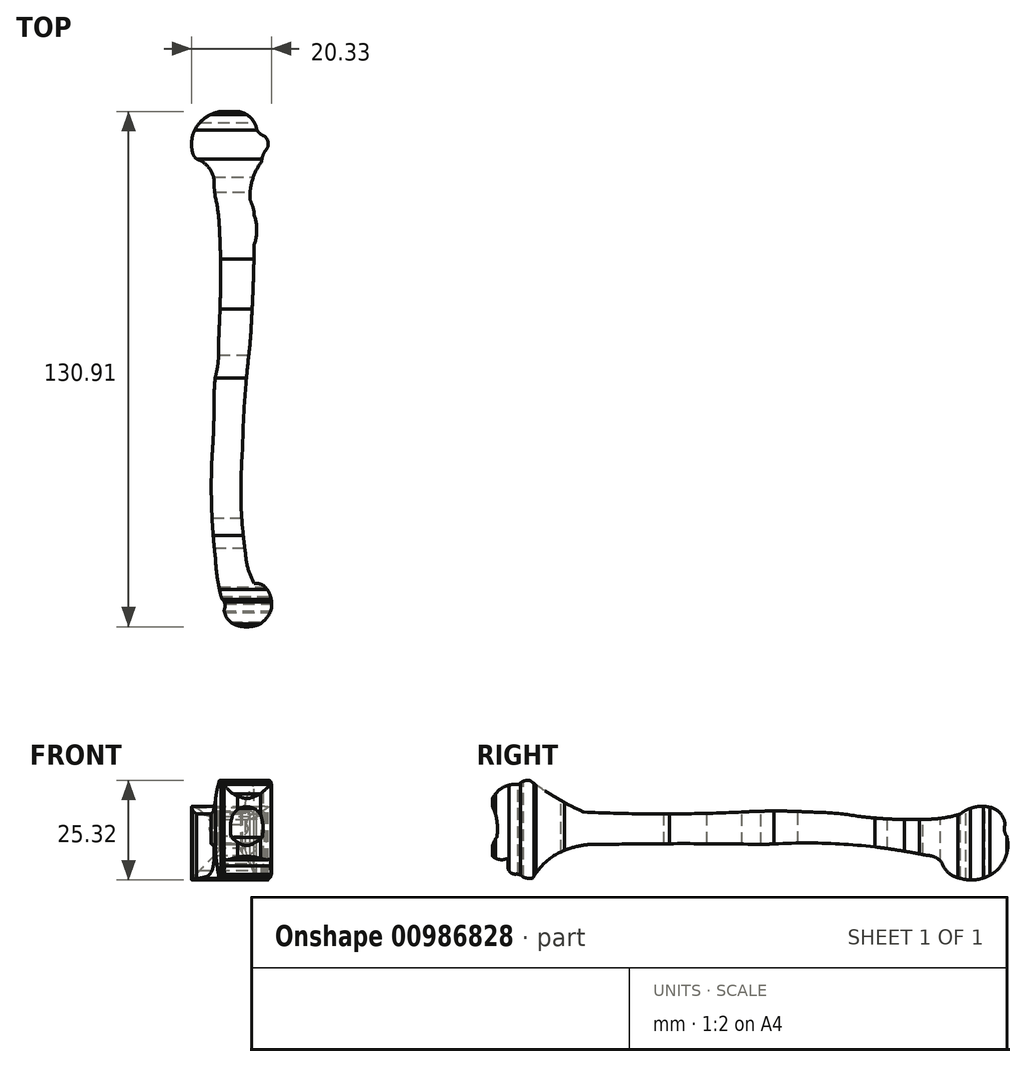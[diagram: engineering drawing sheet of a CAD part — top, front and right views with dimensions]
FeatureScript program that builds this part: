
annotation { "Feature Type Name" : "Feature", "Feature Type Description" : "" }
export const myFeature = defineFeature(function(context is Context, id is Id, definition is map)
    precondition{}
    {
        {
            var Q0;
            Q0=qCreatedBy(makeId("Top.planeOp"),FACE);
            var sketch = newSketch(context, id + "F0", { "sketchPlane" : qUnion([Q0])});
            skSolve(sketch);
        }
        {
            var Q0;
            Q0=qCreatedBy(makeId("Top.planeOp"),FACE);
            var sketch = newSketch(context, id + "F1", { "sketchPlane" : qUnion([Q0])});
            skArc(sketch, "E0", {"start": v(-3.52, 66.02) * mm, "mid": v(-7.2, 63.97) * mm, "end": v(-9.46, 60.42) * mm});
            skArc(sketch, "E1", {"start": v(3.16, 66.02) * mm, "mid": v(-0.18, 66.65) * mm, "end": v(-3.52, 66.02) * mm});
            skArc(sketch, "E2", {"start": v(-9.46, 60.42) * mm, "mid": v(-9.76, 58.04) * mm, "end": v(-9.46, 55.66) * mm});
            skArc(sketch, "E3", {"start": v(-9.46, 55.66) * mm, "mid": v(-9.1, 54.9) * mm, "end": v(-8.52, 54.28) * mm});
            skArc(sketch, "E4", {"start": v(-4.09, 49.15) * mm, "mid": v(-5.6, 52.32) * mm, "end": v(-8.52, 54.28) * mm});
            skArc(sketch, "E5", {"start": v(-4.09, 49.15) * mm, "mid": v(-4.02, 46.94) * mm, "end": v(-3.74, 44.74) * mm});
            skArc(sketch, "E6", {"start": v(-2.67, 35.74) * mm, "mid": v(-2.98, 40.27) * mm, "end": v(-3.74, 44.74) * mm});
            skArc(sketch, "E7", {"start": v(-2.38, 23.8) * mm, "mid": v(-2.43, 29.77) * mm, "end": v(-2.67, 35.74) * mm});
            skArc(sketch, "E8", {"start": v(-2.67, 12.98) * mm, "mid": v(-2.48, 18.39) * mm, "end": v(-2.38, 23.8) * mm});
            skArc(sketch, "E9", {"start": v(-2.67, 12.98) * mm, "mid": v(-2.88, 8.26) * mm, "end": v(-2.96, 3.53) * mm});
            skArc(sketch, "E10", {"start": v(-3.74, -1.22) * mm, "mid": v(-3.23, 1.14) * mm, "end": v(-2.96, 3.53) * mm});
            skArc(sketch, "E11", {"start": v(-3.74, -1.22) * mm, "mid": v(-4.07, -5.7) * mm, "end": v(-4.09, -10.2) * mm});
            skArc(sketch, "E12", {"start": v(-4.55, -21.07) * mm, "mid": v(-4.23, -15.64) * mm, "end": v(-4.09, -10.2) * mm});
            skArc(sketch, "E13", {"start": v(-4.55, -21.07) * mm, "mid": v(-4.69, -34.17) * mm, "end": v(-3.7, -47.24) * mm});
            skArc(sketch, "E14", {"start": v(-3.7, -47.24) * mm, "mid": v(-3.27, -52.02) * mm, "end": v(-2.32, -56.73) * mm});
            skArc(sketch, "E15", {"start": v(-2.32, -56.73) * mm, "mid": v(-2.02, -57.54) * mm, "end": v(-1.48, -58.22) * mm});
            skArc(sketch, "E16", {"start": v(-1.48, -60.4) * mm, "mid": v(-1.26, -59.31) * mm, "end": v(-1.48, -58.22) * mm});
            skArc(sketch, "E17", {"start": v(-1.48, -60.4) * mm, "mid": v(-0.4, -62.89) * mm, "end": v(1.9, -64.3) * mm});
            skArc(sketch, "E18", {"start": v(1.9, -64.3) * mm, "mid": v(4.86, -64.6) * mm, "end": v(7.73, -63.87) * mm});
            skArc(sketch, "E19", {"start": v(7.73, -63.87) * mm, "mid": v(9.34, -62.34) * mm, "end": v(10.43, -60.4) * mm});
            skArc(sketch, "E20", {"start": v(10.43, -60.4) * mm, "mid": v(10.57, -58.97) * mm, "end": v(10.43, -57.53) * mm});
            skArc(sketch, "E21", {"start": v(10.43, -57.53) * mm, "mid": v(9.75, -55.62) * mm, "end": v(8.46, -54.07) * mm});
            skArc(sketch, "E22", {"start": v(8.46, -54.07) * mm, "mid": v(7.35, -53.68) * mm, "end": v(6.17, -53.63) * mm});
            skArc(sketch, "E23", {"start": v(3.98, -46.38) * mm, "mid": v(4.67, -50.13) * mm, "end": v(6.17, -53.63) * mm});
            skArc(sketch, "E24", {"start": v(3.19, -19.72) * mm, "mid": v(2.8, -33.07) * mm, "end": v(3.98, -46.38) * mm});
            skArc(sketch, "E25", {"start": v(5.07, 6.86) * mm, "mid": v(3.76, -6.4) * mm, "end": v(3.19, -19.72) * mm});
            skArc(sketch, "E26", {"start": v(5.07, 6.86) * mm, "mid": v(5.78, 19.65) * mm, "end": v(6.17, 32.46) * mm});
            skArc(sketch, "E27", {"start": v(6.17, 32.46) * mm, "mid": v(6.77, 36.22) * mm, "end": v(6.17, 39.98) * mm});
            skArc(sketch, "E28", {"start": v(6.17, 39.98) * mm, "mid": v(5.84, 41.97) * mm, "end": v(5.07, 43.82) * mm});
            skArc(sketch, "E29", {"start": v(6.76, 61.78) * mm, "mid": v(5.55, 64.4) * mm, "end": v(3.16, 66.02) * mm});
            skArc(sketch, "E30", {"start": v(6.76, 61.78) * mm, "mid": v(7.56, 60.7) * mm, "end": v(8.73, 60.07) * mm});
            skArc(sketch, "E31", {"start": v(9.28, 56.71) * mm, "mid": v(9.69, 58.5) * mm, "end": v(8.73, 60.07) * mm});
            skArc(sketch, "E32", {"start": v(9.28, 56.71) * mm, "mid": v(8.4, 55.25) * mm, "end": v(8.04, 53.58) * mm});
            skArc(sketch, "E33", {"start": v(8.04, 53.58) * mm, "mid": v(5.7, 48.96) * mm, "end": v(5.07, 43.82) * mm});
            skSolve(sketch);
        }
        {
            var Q0;
            Q0=qCreatedBy(makeId("Right.planeOp"),FACE);
            var sketch = newSketch(context, id + "F2", { "sketchPlane" : qUnion([Q0])});
            skArc(sketch, "E34", {"start": v(63.48, -25.15) * mm, "mid": v(65.94, -21.14) * mm, "end": v(65.99, -16.45) * mm});
            skArc(sketch, "E35", {"start": v(54.23, -27.19) * mm, "mid": v(59.12, -27.37) * mm, "end": v(63.48, -25.15) * mm});
            skArc(sketch, "E36", {"start": v(49.6, -23.4) * mm, "mid": v(51.42, -25.9) * mm, "end": v(54.23, -27.19) * mm});
            skArc(sketch, "E37", {"start": v(49.6, -23.4) * mm, "mid": v(47.96, -21.88) * mm, "end": v(45.78, -21.37) * mm});
            skArc(sketch, "E38", {"start": v(65.57, -13.52) * mm, "mid": v(65.4, -15.03) * mm, "end": v(65.99, -16.45) * mm});
            skArc(sketch, "E39", {"start": v(65.57, -13.52) * mm, "mid": v(64.36, -10.62) * mm, "end": v(61.62, -9.1) * mm});
            skArc(sketch, "E40", {"start": v(61.62, -9.1) * mm, "mid": v(57.72, -9.1) * mm, "end": v(54.23, -10.84) * mm});
            skArc(sketch, "E41", {"start": v(46.71, -12.16) * mm, "mid": v(50.51, -11.74) * mm, "end": v(54.23, -10.84) * mm});
            skArc(sketch, "E42", {"start": v(45.78, -21.37) * mm, "mid": v(25.17, -18.55) * mm, "end": v(4.38, -18.58) * mm});
            skArc(sketch, "E43", {"start": v(4.38, -18.58) * mm, "mid": v(-16.31, -18.36) * mm, "end": v(-37, -18.58) * mm});
            skArc(sketch, "E44", {"start": v(-37, -18.58) * mm, "mid": v(-40.84, -18.66) * mm, "end": v(-44.6, -19.45) * mm});
            skArc(sketch, "E45", {"start": v(-44.6, -19.45) * mm, "mid": v(-50.3, -22.33) * mm, "end": v(-54.45, -27.19) * mm});
            skArc(sketch, "E46", {"start": v(-60.75, -24) * mm, "mid": v(-60.66, -23.06) * mm, "end": v(-61, -22.19) * mm});
            skArc(sketch, "E47", {"start": v(-64.85, -21.37) * mm, "mid": v(-63.06, -22.38) * mm, "end": v(-61, -22.19) * mm});
            skArc(sketch, "E48", {"start": v(-63.55, -16.72) * mm, "mid": v(-64.64, -18.92) * mm, "end": v(-64.85, -21.37) * mm});
            skArc(sketch, "E49", {"start": v(-63.55, -16.72) * mm, "mid": v(-63.45, -13) * mm, "end": v(-64.44, -9.4) * mm});
            skArc(sketch, "E50", {"start": v(-63.93, -5.77) * mm, "mid": v(-64.77, -7.5) * mm, "end": v(-64.44, -9.4) * mm});
            skArc(sketch, "E51", {"start": v(-60.75, -24) * mm, "mid": v(-60.25, -25.52) * mm, "end": v(-58.78, -26.13) * mm});
            skArc(sketch, "E52", {"start": v(-56.87, -26.86) * mm, "mid": v(-57.73, -26.24) * mm, "end": v(-58.78, -26.13) * mm});
            skArc(sketch, "E53", {"start": v(-56.87, -26.86) * mm, "mid": v(-55.68, -27.16) * mm, "end": v(-54.45, -27.19) * mm});
            skArc(sketch, "E54", {"start": v(-58.3, -3.32) * mm, "mid": v(-61.43, -3.82) * mm, "end": v(-63.93, -5.77) * mm});
            skArc(sketch, "E55", {"start": v(-58.3, -3.32) * mm, "mid": v(-57.93, -3.26) * mm, "end": v(-57.66, -3) * mm});
            skArc(sketch, "E56", {"start": v(-55.12, -2.33) * mm, "mid": v(-56.46, -2.39) * mm, "end": v(-57.66, -3) * mm});
            skArc(sketch, "E57", {"start": v(-55.12, -2.33) * mm, "mid": v(-48.5, -6.71) * mm, "end": v(-41.43, -10.35) * mm});
            skArc(sketch, "E58", {"start": v(-41.43, -10.35) * mm, "mid": v(-21.42, -10.82) * mm, "end": v(-1.42, -10.35) * mm});
            skArc(sketch, "E59", {"start": v(28.79, -11.49) * mm, "mid": v(37.74, -12.18) * mm, "end": v(46.71, -12.16) * mm});
            skArc(sketch, "E60", {"start": v(16.1, -10.35) * mm, "mid": v(7.34, -10.08) * mm, "end": v(-1.42, -10.35) * mm});
            skArc(sketch, "E61", {"start": v(28.79, -11.49) * mm, "mid": v(22.47, -10.66) * mm, "end": v(16.1, -10.35) * mm});
            skSolve(sketch);
        }
        {
            var Q0;
            Q0 = qSketchRegion(id + "F1", true);
            extrude(context, id + "F3", {"entities" : qUnion([Q0]), "oppositeDirection" : true, "depth" : 35.56 * mm, "offsetDistance" : 25.4 * mm});
        }
        {
            var Q0;
            Q0 = qSketchRegion(id + "F2", true);
            extrude(context, id + "F4", {"entities" : qUnion([Q0]), "operationType" : NewBodyOperationType.INTERSECT, "oppositeDirection" : true, "depth" : 25.4 * mm, "offsetDistance" : 25.4 * mm, "hasSecondDirection" : true, "secondDirectionOppositeDirection" : false, "secondDirectionDepth" : 25.4 * mm});
        }
    });
